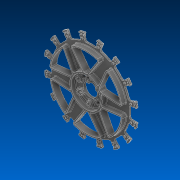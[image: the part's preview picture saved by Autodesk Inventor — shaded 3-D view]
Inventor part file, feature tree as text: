
AUTODESK INVENTOR PART (.ipt)
format: ipt  version: 2022.2 (Build 262287000, 287)  size: 2,174,976 bytes
history: native  units: in
note: dims shown in document units (in); Inventor stores cm internally (conversion verified against a paired STEP export)
features: fillet x1
ambient origin geometry x8: Origin, YZ Plane, XZ Plane, XY Plane, X Axis, Y Axis, Z Axis, Center Point
bodies: Solid1 (feature_tree)
feature tree (1):
  fillet  "Fillet16"  [1 undecoded]
note: 1 required parameter value undecoded (feature->parameter linkage not recoverable at this tier; creation-order binding heuristic only, values carry confidence <= 0.55)
